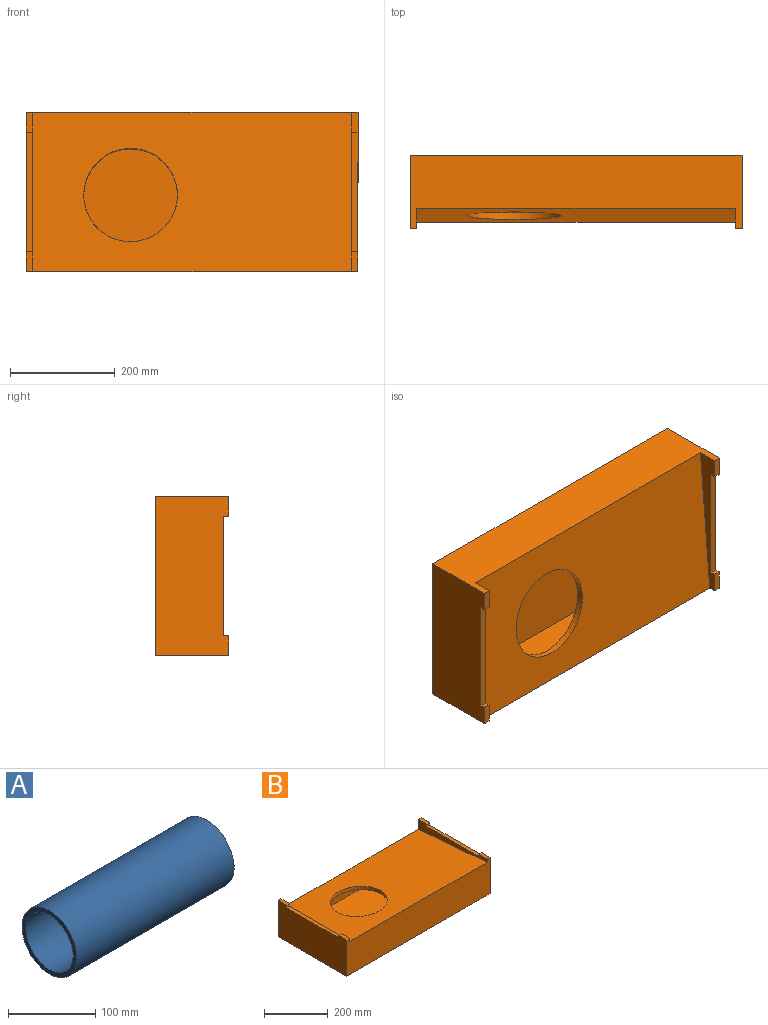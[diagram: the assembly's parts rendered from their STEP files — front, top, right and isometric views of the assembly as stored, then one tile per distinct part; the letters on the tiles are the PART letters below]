
ASSEMBLY  parts=2 mates=1
PART A: 4 faces, bbox 254x88.9x88.9 mm
  f0: cylinder r=38.1mm len=254mm, axis (1,0,0), area 60804.9mm2, adj f2,f3
  f1: cylinder r=44.45mm len=254mm, axis (1,0,0), area 70939mm2, adj f2,f3
  f2: plane 88.9x88.9mm, normal (-1,0,0), area 1646.8mm2, adj f0,f1
  f3: plane 88.9x88.9mm, normal (1,0,0), area 1646.8mm2, adj f0,f1
PART B: 26 faces, bbox 635x304.8x139.7 mm
  f0: plane 609.6x304.8mm, normal (0,0.08,1), area 161265.5mm2, adj f2,f4,f6,f19,f25
  f1: plane 304.8x139.7mm, normal (1,0,0), area 34179.8mm2, adj f2,f4,f5,f13,f14,f15,f16,f17
  f2: plane 635x139.7mm, normal (0,1,0), area 65483.7mm2, adj f0,f1,f3,f5,f15,f19,f24,f25
  f3: plane 304.8x139.7mm, normal (-1,0,0), area 40387mm2, adj f2,f4,f5,f20,f21,f22,f23,f24
  f4: plane 635x139.7mm, normal (0,-1,0), area 80967.6mm2, adj f0,f1,f3,f5,f14,f19,f20,f25
  f5: plane 635x304.8mm, normal (0,0,-1), area 193548mm2, adj f1,f2,f3,f4
  f6: cylinder r=89.53mm len=179.51mm, axis (0,0.08,1), area 7144.6mm2, adj f0,f12
  f7: plane 279.4x100.5mm, normal (-1,0,0), area 18619.2mm2, adj f8,f10,f11,f12,f13
  f8: plane 609.6x77.21mm, normal (0,-1,0), area 47069.8mm2, adj f7,f9,f11,f12
  f9: plane 279.4x100.5mm, normal (1,0,0), area 24826.4mm2, adj f8,f10,f11,f12
  f10: plane 609.6x100.5mm, normal (0,1,0), area 61263.4mm2, adj f7,f9,f11,f12
  f11: plane 609.6x279.4mm, normal (0,0,1), area 170322.2mm2, adj f7,f8,f9,f10
  f12: plane 609.6x279.4mm, normal (0,-0.08,-1), area 145728mm2, adj f6,f7,f8,f9,f10
  f13: cylinder r=44.45mm len=88.9mm, axis (1,0,0), area 3547mm2, adj f1,f7
  f14: plane 38.1x12.7mm, normal (0,0,1), area 483.9mm2, adj f1,f4,f18,f19
  f15: plane 38.1x12.7mm, normal (0,0,1), area 483.9mm2, adj f1,f2,f16,f19
  f16: plane 12.7x9.6mm, normal (0,-1,0), area 121.9mm2, adj f1,f15,f17,f19
  f17: plane 228.6x12.7mm, normal (0,0,1), area 2903.2mm2, adj f1,f16,f18,f19
  f18: plane 12.7x9.6mm, normal (0,1,0), area 121.9mm2, adj f1,f14,f17,f19
  f19: plane 304.8x38.1mm, normal (-1,0,0), area 5548.4mm2, adj f0,f2,f4,f14,f15,f16,f17,f18
  f20: plane 38.1x12.7mm, normal (0,0,1), area 483.9mm2, adj f3,f4,f21,f25
  f21: plane 12.7x9.6mm, normal (0,1,0), area 121.9mm2, adj f3,f20,f22,f25
  f22: plane 228.6x12.7mm, normal (0,0,1), area 2903.2mm2, adj f3,f21,f23,f25
  f23: plane 12.7x9.6mm, normal (0,-1,0), area 121.9mm2, adj f3,f22,f24,f25
  f24: plane 38.1x12.7mm, normal (0,0,1), area 483.9mm2, adj f2,f3,f23,f25
  f25: plane 304.8x38.1mm, normal (1,0,0), area 5548.4mm2, adj f0,f2,f4,f20,f21,f22,f23,f24
PLACE A rot(axis=(1,0,0),90deg) t=(339.87,130.57,89.5)mm
PLACE B rot(axis=(1,0,0),90deg) t=(22.37,191.16,172.11)mm fixed
MATE cylindrical B.f13 <-> A.f0  axis (1,0,0) through (339.87,130.57,89.5)mm
